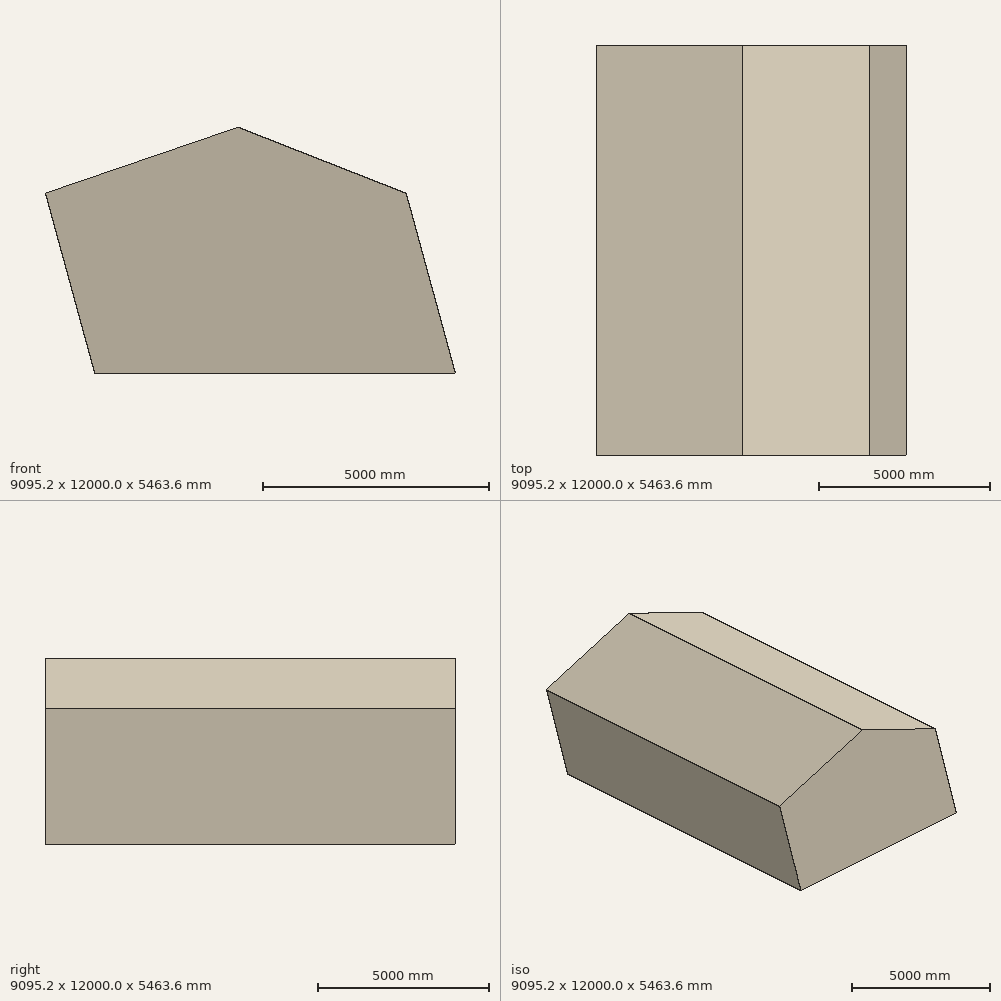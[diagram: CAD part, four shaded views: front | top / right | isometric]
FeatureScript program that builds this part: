
annotation { "Feature Type Name" : "Feature", "Feature Type Description" : "" }
export const myFeature = defineFeature(function(context is Context, id is Id, definition is map)
    precondition{}
    {
        {
            var Q0;
            Q0=qCreatedBy(makeId("Front.planeOp"),FACE);
            var sketch = newSketch(context, id + "F0", { "sketchPlane" : qUnion([Q0])});
            skLineSegment(sketch, "E0.bottom", {"start": v(4547.62, -2000) * mm, "end": v(-3452.38, -2000) * mm});
            skLineSegment(sketch, "E0.left", {"start": v(4547.62, -2000) * mm, "end": v(3452.38, 2000) * mm});
            skLineSegment(sketch, "E0.right", {"start": v(-3452.38, -2000) * mm, "end": v(-4547.62, 2000) * mm});
            skPoint(sketch, "E0.middle", {"position": v(0, 0) * mm});
            skLineSegment(sketch, "E1", {"start": v(-4547.62, 2000) * mm, "end": v(-270.24, 3463.6) * mm});
            skLineSegment(sketch, "E2", {"start": v(3452.38, 2000) * mm, "end": v(-270.24, 3463.6) * mm});
            skSolve(sketch);
        }
        {
            var Q0;
            Q0=makeQuery(id+"F0.imprint","IMPRINT",FACE,{"disambiguationData":[TD([[makeQuery(id+"F0.imprint","IMPRINT",EDGE,{"derivedFrom":sQuery(id+"F0.wireOp",EDGE,"E0.bottom")}),-1.0]])]});
            extrude(context, id + "F1", {"entities" : qUnion([Q0]), "depth" : 12000 * mm});
        }
    });
